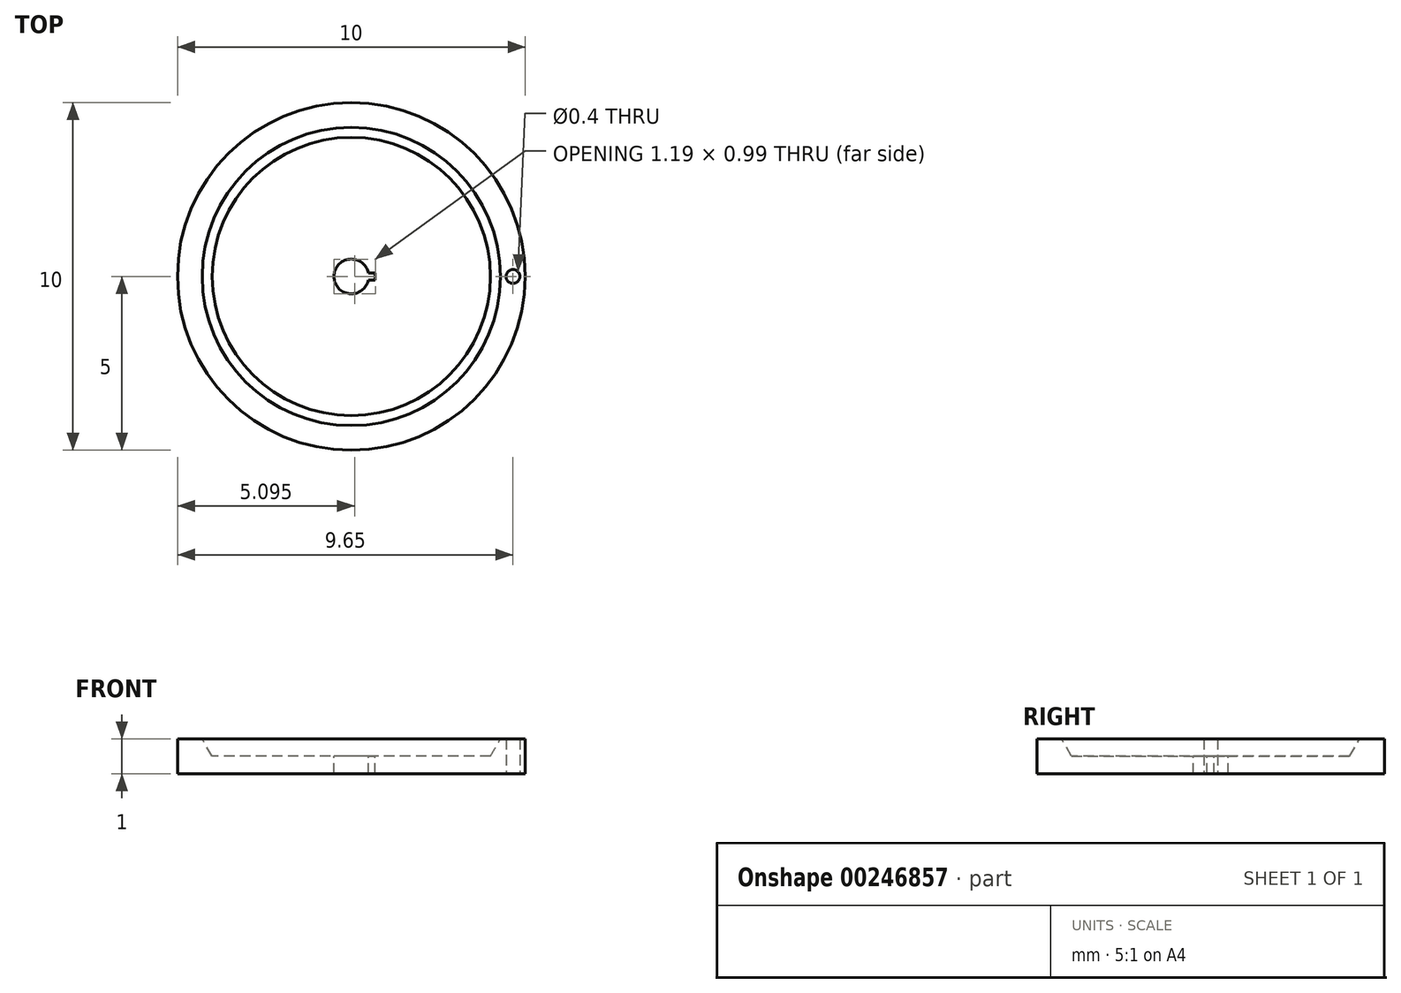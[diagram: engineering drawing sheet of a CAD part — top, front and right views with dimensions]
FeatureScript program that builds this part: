
annotation { "Feature Type Name" : "Feature", "Feature Type Description" : "" }
export const myFeature = defineFeature(function(context is Context, id is Id, definition is map)
    precondition{}
    {
        {
            var Q0;
            Q0=qCreatedBy(makeId("Top.planeOp"),FACE);
            var sketch = newSketch(context, id + "F0", { "sketchPlane" : qUnion([Q0])});
            skCircle(sketch, "E0", {"center": v(0, 0) * mm, "radius": 5 * mm});
            skCircle(sketch, "E1", {"center": v(0, 0) * mm, "radius": 4 * mm});
            skCircle(sketch, "E2", {"center": v(4.65, 0) * mm, "radius": 0.2 * mm});
            skPoint(sketch, "E2.first.point", {"position": v(4, 0) * mm});
            skPoint(sketch, "E2.second.point", {"position": v(4.85, 0) * mm});
            skPoint(sketch, "E2.third.point", {"position": v(4.47, 0.08) * mm});
            skSolve(sketch);
        }
        {
            var Q0;
            Q0=makeQuery(id+"F0.imprint","IMPRINT",FACE,{"disambiguationData":[TD([[makeQuery(id+"F0.imprint","IMPRINT",EDGE,{"derivedFrom":sQuery(id+"F0.wireOp",EDGE,"E0")}),1.0]])]});
            extrude(context, id + "F1", {"entities" : qUnion([Q0]), "depth" : 1 * mm});
        }
        {
            var Q0;
            Q0=makeQuery(id+"F0.imprint","IMPRINT",FACE,{"disambiguationData":[TD([[makeQuery(id+"F0.imprint","IMPRINT",EDGE,{"derivedFrom":sQuery(id+"F0.wireOp",EDGE,"E1")}),1.0]])]});
            extrude(context, id + "F2", {"entities" : qUnion([Q0]), "operationType" : NewBodyOperationType.ADD, "depth" : 0.5 * mm});
        }
        {
            var Q0;
            Q0=makeQuery(id+"F2.opExtrude","CAP_FACE",FACE,{"disambiguationData":[OSD([sQuery(id+"F0.wireOp",EDGE,"E1")])],"isStart":false});
            var sketch = newSketch(context, id + "F3", { "sketchPlane" : qUnion([Q0])});
            skCircle(sketch, "E3", {"center": v(0, 0) * mm, "radius": 0.5 * mm});
            skPoint(sketch, "E3.centerSnap0", {"position": v(-6.64, 0) * mm});
            skLineSegment(sketch, "E4", {"start": v(0.49, 0.1) * mm, "end": v(0.69, 0.1) * mm});
            skLineSegment(sketch, "E5", {"start": v(0.69, 0.1) * mm, "end": v(0.69, 0) * mm});
            skLineSegment(sketch, "E6", {"start": v(0.69, 0) * mm, "end": v(0.69, -0.1) * mm});
            skLineSegment(sketch, "E7", {"start": v(0.69, -0.1) * mm, "end": v(0.49, -0.1) * mm});
            skSolve(sketch);
        }
        {
            var Q0;
            {var subQ0=sQuery(id+"F3.wireOp",EDGE,"E3");var subQ1=makeQuery(id+"F3.imprint","INTERSECT",VERTEX,{"derivedFrom":[subQ0,sQuery(id+"F3.wireOp",EDGE,"E4")]});Q0=makeQuery(id+"F3.imprint","IMPRINT",FACE,{"disambiguationData":[TD([[makeQuery(id+"F3.imprint","IMPRINT",EDGE,{"disambiguationData":[TD([[subQ1,-1.0]])],"derivedFrom":subQ0}),1.0]])]});}
            var Q1;
            {var subQ0=sQuery(id+"F3.wireOp",EDGE,"E4");Q1=makeQuery(id+"F3.imprint","IMPRINT",FACE,{"disambiguationData":[TD([[makeQuery(id+"F3.imprint","IMPRINT",EDGE,{"derivedFrom":subQ0}),-1.0]])]});}
            extrude(context, id + "F4", {"entities" : qUnion([Q0, Q1]), "operationType" : NewBodyOperationType.REMOVE, "oppositeDirection" : true, "depth" : 25 * mm});
        }
        {
            var Q0;
            Q0=makeQuery(id+"F1.opExtrude","CAP_EDGE",EDGE,{"disambiguationData":[OSD([sQuery(id+"F0.wireOp",EDGE,"E1")])],"isStart":false});
            chamfer(context, id + "F5", {"entities" : qUnion([Q0]), "chamferType" : ChamferType.OFFSET_ANGLE, "width" : 0.5 * mm, "oppositeDirection" : false, "angle" : 30 * degree, "tangentPropagation" : true});
        }
    });
